# Revit family: Bottle Filling Station_Mechanical_Single-Elkay-LZLMSN-EDFPVM214DK &EZLMSN-EDFPVM214DK
name_source: partatom
category: Plumbing Fixtures
units: mm (PartAtom-declared; Revit-internal decimal feet)

## family parameters
Cut with Voids When Loaded = No
Host = Face
Maintain Annotation Orientation = No
OmniClass Number = 23.65.70.14.11
OmniClass Title = Drinking Fountains/Coolers
Part Type = Normal
Room Calculation Point = No
Round Connector Dimension = Use Diameter
Shared = No

## types (4) — shared parameters
Activation Method = Mechanical Bottle Filler Button with Mechanical Front Bubbler Button
Assembly Code = D2010810
Default Elevation = 48 "
Height = 34.63 "
Inlet Connection = 0.38 "
Length = 19.75 "
Manufacturer Brand = Elkay (by Zurn Elkay Water Solutions)
Material = Finish-Elkay-Stainless Steel
Outlet Connection = 1.5 "
Product Documentation Link = https://www.elkayfiles.com
Product Installation Sheet URL = https://www.elkayfiles.com
Product Page URL = https://www.elkay.com
Secondary Material = Elkay-Transparent
URL = https://www.elkay.com
Width = 19 "
zero-valued in all types: Approx. Shipping Weight (lbs), Product Weight (lbs)

## per-type parameters (varying)
| type | Description | EZLMSN-EDFPVM214DK | LZLMSN-EDFPVM214DK | Manufacturer | Model | Repair Parts URL |
| LZLMSN-EDFPVM214DK(Mechanical Bottle Filling Station with ntegral Soft Sides® Fountain ) | ezH2O® Vandal Resistant Mechanical Bottle Filling Station with Integral Soft Sides® Fountain Filtered Non-Refrigerated Stainless | No | No | (Elkay Manufacturer Company) | LZLMSN-EDFPVM214DK | https://www.elkay.com |
| EZLMSN-EDFPVM214DK(Mechanical Bottle Filling Station with ntegral Soft Sides® Fountain) | ezH2O® Vandal Resistant Mechanical Bottle Filling Station with Integral Soft Sides® Fountain Non-Filtered Non-Refrigerated Stainless | Yes | No | Elkay Manufacturer Company | EZLMSN-EDFPVM214DK | https://www.elkayfiles.com |
| EZLMSN-EDFPVM214DK(Mechanical Bottle Filling Station with ntegral Soft Sides® Fountain) ( Optional Panel) | ezH2O® Vandal Resistant Mechanical Bottle Filling Station with Integral Soft Sides® Fountain Non-Filtered Non-Refrigerated Stainless | No | Yes | Elkay Manufacturer Company | EZLMSN-EDFPVM214DK | https://www.elkayfiles.com |
| LZLMSN-EDFPVM214DK(Mechanical Bottle Filling Station with ntegral Soft Sides® Fountain ) ( Optional Panel) | ezH2O® Vandal Resistant Mechanical Bottle Filling Station with Integral Soft Sides® Fountain Filtered Non-Refrigerated Stainless | No | Yes | (Elkay Manufacturer Company) | LZLMSN-EDFPVM214DK | https://www.elkay.com |

## geometry (parser evidence)
native form markers: Sweep x15
no freeform markers — native parametric forms only
